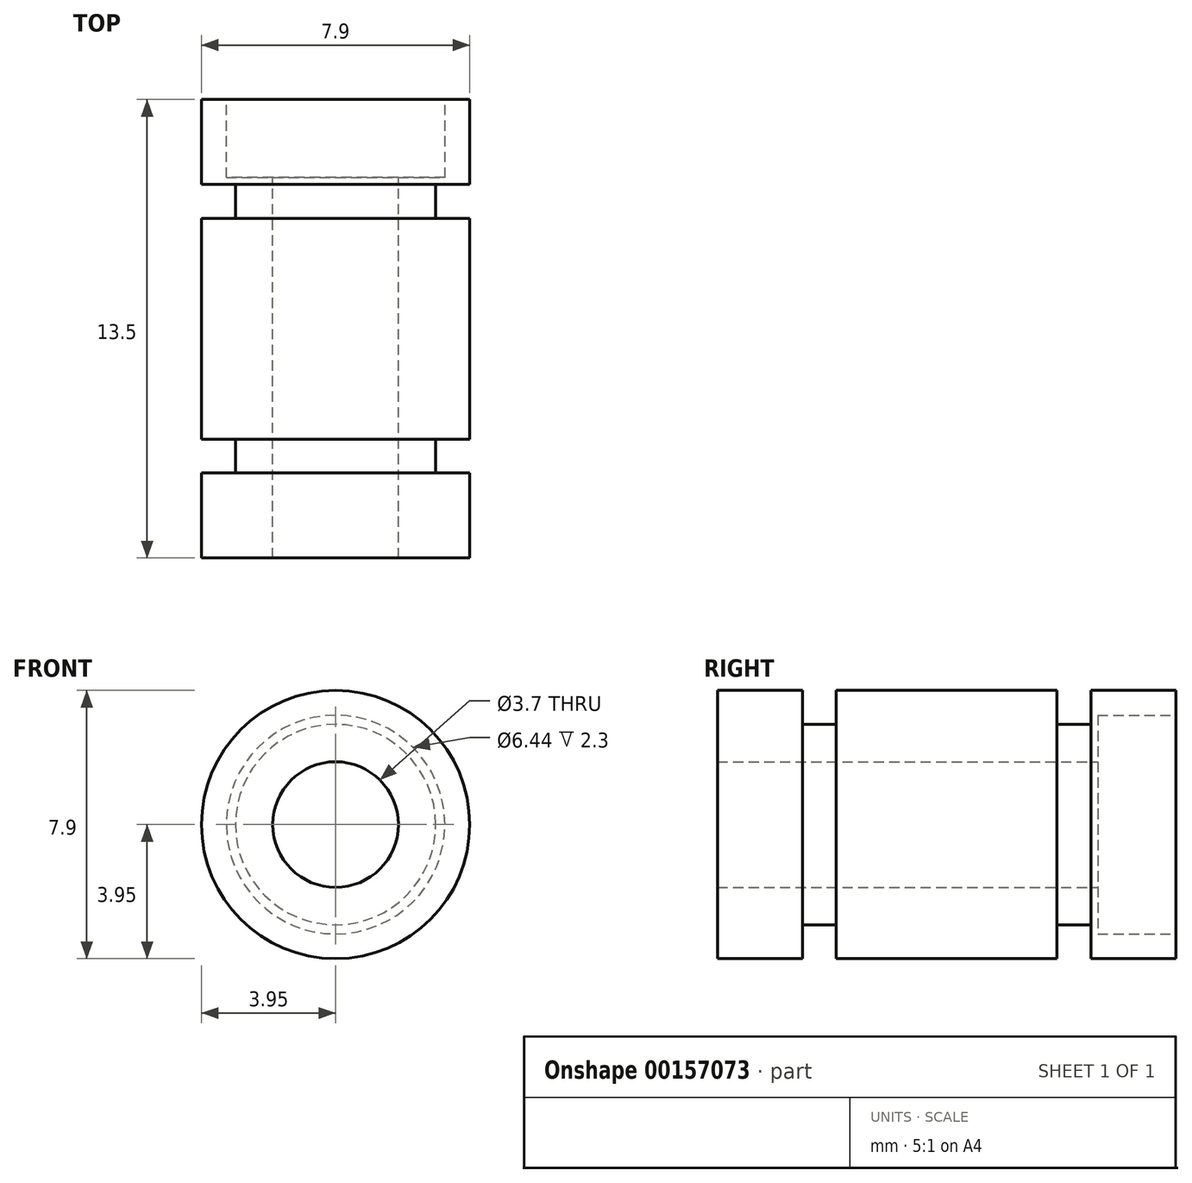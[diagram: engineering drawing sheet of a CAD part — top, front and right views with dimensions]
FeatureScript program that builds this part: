
annotation { "Feature Type Name" : "Feature", "Feature Type Description" : "" }
export const myFeature = defineFeature(function(context is Context, id is Id, definition is map)
    precondition{}
    {
        {
            var Q0;
            Q0=qCreatedBy(makeId("Right.planeOp"),FACE);
            var sketch = newSketch(context, id + "F0", { "sketchPlane" : qUnion([Q0])});
            skLineSegment(sketch, "E0", {"start": v(11.47, 0) * mm, "end": v(0, 0) * mm, "construction": true});
            skLineSegment(sketch, "E1", {"start": v(11.2, 1.85) * mm, "end": v(0, 1.85) * mm});
            skLineSegment(sketch, "E2", {"start": v(11.2, 1.85) * mm, "end": v(11.2, 3.22) * mm});
            skLineSegment(sketch, "E3", {"start": v(13.5, 3.22) * mm, "end": v(11.2, 3.22) * mm});
            skLineSegment(sketch, "E4", {"start": v(13.5, 3.22) * mm, "end": v(13.5, 3.95) * mm});
            skLineSegment(sketch, "E5", {"start": v(11, 3.95) * mm, "end": v(13.5, 3.95) * mm});
            skLineSegment(sketch, "E6", {"start": v(11, 3.95) * mm, "end": v(11, 2.95) * mm});
            skLineSegment(sketch, "E7", {"start": v(10, 2.95) * mm, "end": v(11, 2.95) * mm});
            skLineSegment(sketch, "E8", {"start": v(2.5, 2.95) * mm, "end": v(2.5, 3.95) * mm});
            skLineSegment(sketch, "E9", {"start": v(0, 3.95) * mm, "end": v(2.5, 3.95) * mm});
            skLineSegment(sketch, "E10", {"start": v(0, 3.95) * mm, "end": v(0, 1.85) * mm});
            skLineSegment(sketch, "E11", {"start": v(3.5, 2.95) * mm, "end": v(3.5, 3.95) * mm});
            skLineSegment(sketch, "E12", {"start": v(3.5, 3.95) * mm, "end": v(10, 3.95) * mm});
            skLineSegment(sketch, "E13", {"start": v(10, 3.95) * mm, "end": v(10, 2.95) * mm});
            skLineSegment(sketch, "E14.trimOffspring", {"start": v(3.5, 2.95) * mm, "end": v(2.5, 2.95) * mm});
            skSolve(sketch);
        }
        {
            var Q0;
            Q0=makeQuery(id+"F0.imprint","IMPRINT",FACE,{"disambiguationData":[TD([[makeQuery(id+"F0.imprint","IMPRINT",EDGE,{"derivedFrom":sQuery(id+"F0.wireOp",EDGE,"E1")}),-1.0]])]});
            var Q1;
            Q1=sQuery(id+"F0.wireOp",EDGE,"E0");
            revolve(context, id + "F1", {"entities" : qUnion([Q0]), "axis" : qUnion([Q1]), "revolveType" : RevolveType.FULL});
        }
    });
